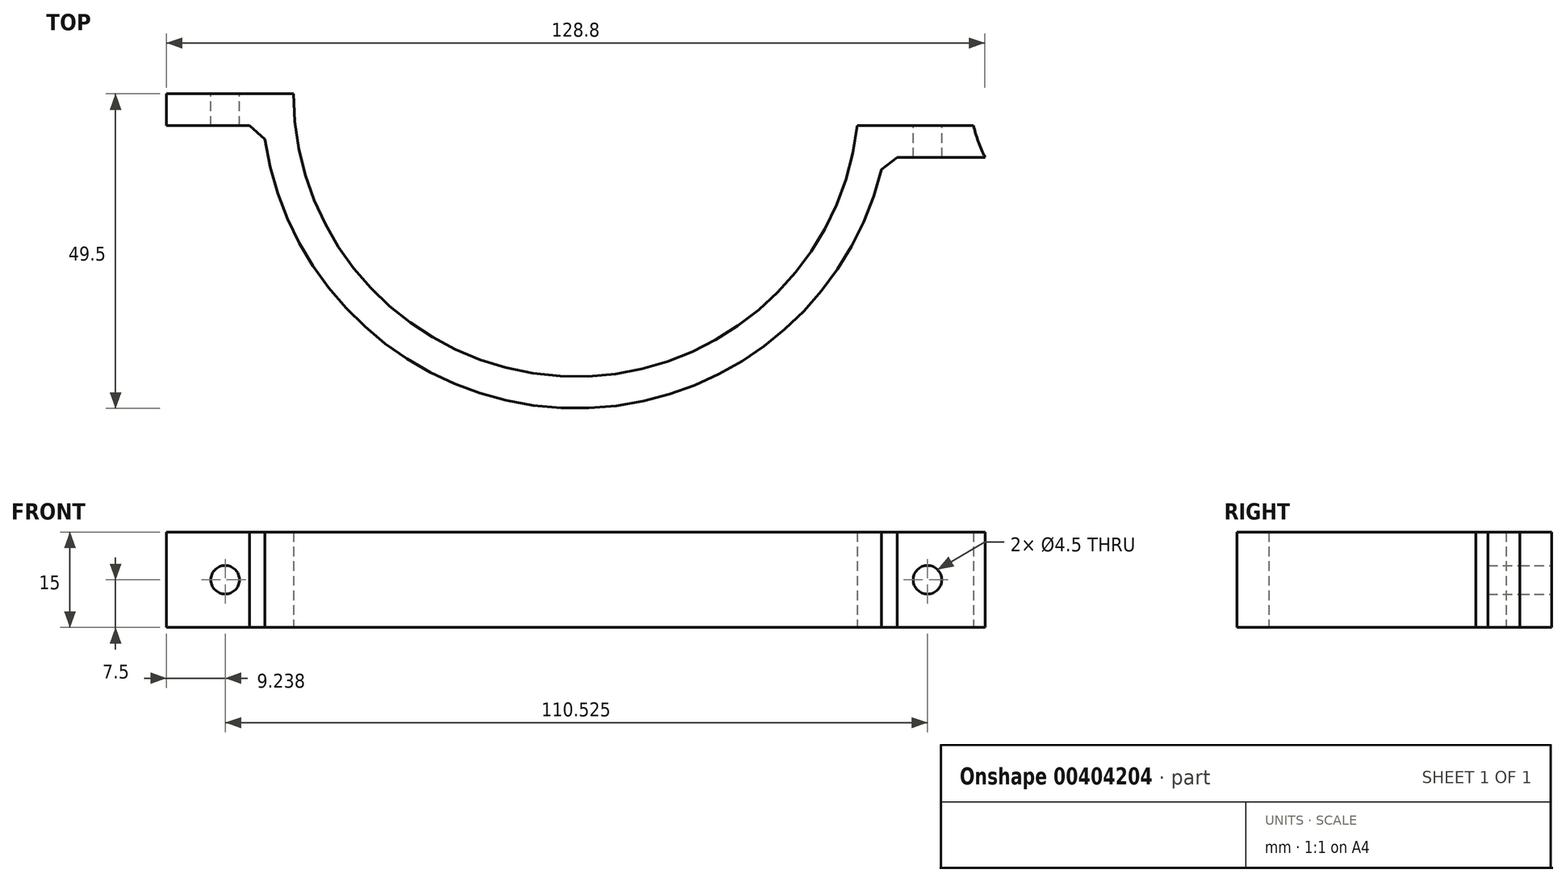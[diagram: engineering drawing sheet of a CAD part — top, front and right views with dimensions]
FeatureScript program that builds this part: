
annotation { "Feature Type Name" : "Feature", "Feature Type Description" : "" }
export const myFeature = defineFeature(function(context is Context, id is Id, definition is map)
    precondition{}
    {
        {
            var Q0;
            Q0=qCreatedBy(makeId("Top.planeOp"),FACE);
            var sketch = newSketch(context, id + "F0", { "sketchPlane" : qUnion([Q0])});
            skArc(sketch, "E0", {"start": v(44.5, 0) * mm, "mid": v(-44.43, 2.5) * mm, "end": v(44.22, -5) * mm, "construction": true});
            skArc(sketch, "E1", {"start": v(-44.5, 0) * mm, "mid": v(-2.5, -44.43) * mm, "end": v(44.22, -5) * mm});
            skLineSegment(sketch, "E2", {"start": v(-44.5, 0) * mm, "end": v(-64.5, 0) * mm});
            skLineSegment(sketch, "E3", {"start": v(-64.5, 0) * mm, "end": v(-64.5, -5) * mm});
            skLineSegment(sketch, "E4", {"start": v(-64.5, -5) * mm, "end": v(-49.25, -5) * mm});
            skArc(sketch, "E5", {"start": v(47.76, -13) * mm, "mid": v(-4.07, -49.33) * mm, "end": v(-49.25, -5) * mm});
            skLineSegment(sketch, "E6.MirrorCS", {"start": v(44.5, 0) * mm, "end": v(64.5, 0) * mm, "construction": true});
            skLineSegment(sketch, "E7", {"start": v(64.5, 0) * mm, "end": v(64.5, -5) * mm, "construction": true});
            skLineSegment(sketch, "E8", {"start": v(62.5, -5) * mm, "end": v(49.25, -5) * mm});
            skPoint(sketch, "E9.orphan", {"position": v(49.25, -5) * mm});
            skLineSegment(sketch, "E10", {"start": v(44.22, -5) * mm, "end": v(49.25, -5) * mm});
            skLineSegment(sketch, "E11", {"start": v(64.5, -5) * mm, "end": v(64.5, -13) * mm, "construction": true});
            skLineSegment(sketch, "E12", {"start": v(64.5, -13) * mm, "end": v(47.76, -13) * mm});
            skArc(sketch, "E13", {"start": v(67.67, -5) * mm, "mid": v(69.7, -9.36) * mm, "end": v(72.84, -13) * mm, "construction": true});
            skArc(sketch, "E14", {"start": v(62.5, -5) * mm, "mid": v(63.91, -9.18) * mm, "end": v(66.12, -13) * mm});
            skLineSegment(sketch, "E15", {"start": v(66.12, -13) * mm, "end": v(64.5, -13) * mm});
            skSolve(sketch);
        }
        {
            var Q0;
            Q0=qSketchRegion(id+"F0",true);
            extrude(context, id + "F1", {"entities" : qUnion([Q0]), "endBound" : BoundingType.SYMMETRIC, "depth" : 15 * mm});
        }
        {
            var Q0;
            Q0=makeQuery(id+"F1.opExtrude","SWEPT_FACE",FACE,{"disambiguationData":[OSD([sQuery(id+"F0.wireOp",EDGE,"E2")])]});
            var sketch = newSketch(context, id + "F2", { "sketchPlane" : qUnion([Q0])});
            skCircle(sketch, "E16", {"center": v(-55.26, 0) * mm, "radius": 2.25 * mm});
            skCircle(sketch, "E17.MirrorC", {"center": v(55.26, 0) * mm, "radius": 2.25 * mm});
            skSolve(sketch);
        }
        {
            var Q0;
            Q0=qSketchRegion(id+"F2",true);
            extrude(context, id + "F3", {"entities" : qUnion([Q0]), "operationType" : NewBodyOperationType.REMOVE, "oppositeDirection" : true, "depth" : 25 * mm});
        }
        {
            var Q0;
            Q0=makeQuery(id+"F1.opExtrude","CAP_FACE",FACE,{"disambiguationData":[OSD([sQuery(id+"F0.wireOp",EDGE,"E1"),sQuery(id+"F0.wireOp",EDGE,"E2"),sQuery(id+"F0.wireOp",EDGE,"E3"),sQuery(id+"F0.wireOp",EDGE,"E4"),sQuery(id+"F0.wireOp",EDGE,"E5"),sQuery(id+"F0.wireOp",EDGE,"E8"),sQuery(id+"F0.wireOp",EDGE,"E10"),sQuery(id+"F0.wireOp",EDGE,"E12"),sQuery(id+"F0.wireOp",EDGE,"E14"),sQuery(id+"F0.wireOp",EDGE,"E15")])],"isStart":false});
            var sketch = newSketch(context, id + "F4", { "sketchPlane" : qUnion([Q0])});
            skArc(sketch, "E18", {"start": v(47.76, -13) * mm, "mid": v(48.14, -11.5) * mm, "end": v(48.48, -10) * mm});
            skLineSegment(sketch, "E19", {"start": v(48.48, -10) * mm, "end": v(66.12, -10) * mm});
            skLineSegment(sketch, "E20", {"start": v(66.12, -10) * mm, "end": v(66.12, -13) * mm});
            skLineSegment(sketch, "E21", {"start": v(66.12, -13) * mm, "end": v(47.76, -13) * mm});
            skSolve(sketch);
        }
        {
            var Q0;
            Q0 = qSketchRegion(id + "F4", true);
            extrude(context, id + "F5", {"entities" : qUnion([Q0]), "operationType" : NewBodyOperationType.REMOVE, "oppositeDirection" : true, "depth" : 25 * mm});
        }
        {
            var Q0;
            Q0=makeQuery(id+"F5.boolean.opBoolean","COPY",EDGE,{"derivedFrom":makeQuery(id+"F5.opExtrude","SWEPT_EDGE",EDGE,{"disambiguationData":[OSD([sQuery(id+"F4.wireOp",EDGE,"E18"),sQuery(id+"F4.wireOp",EDGE,"E19")])]})});
            var Q1;
            Q1=makeQuery(id+"F1.opExtrude","SWEPT_EDGE",EDGE,{"disambiguationData":[OSD([sQuery(id+"F0.wireOp",EDGE,"E4"),sQuery(id+"F0.wireOp",EDGE,"E5")])]});
            chamfer(context, id + "F6", {"entities" : qUnion([Q0, Q1]), "width" : 2.5 * mm, "tangentPropagation" : true});
        }
    });
